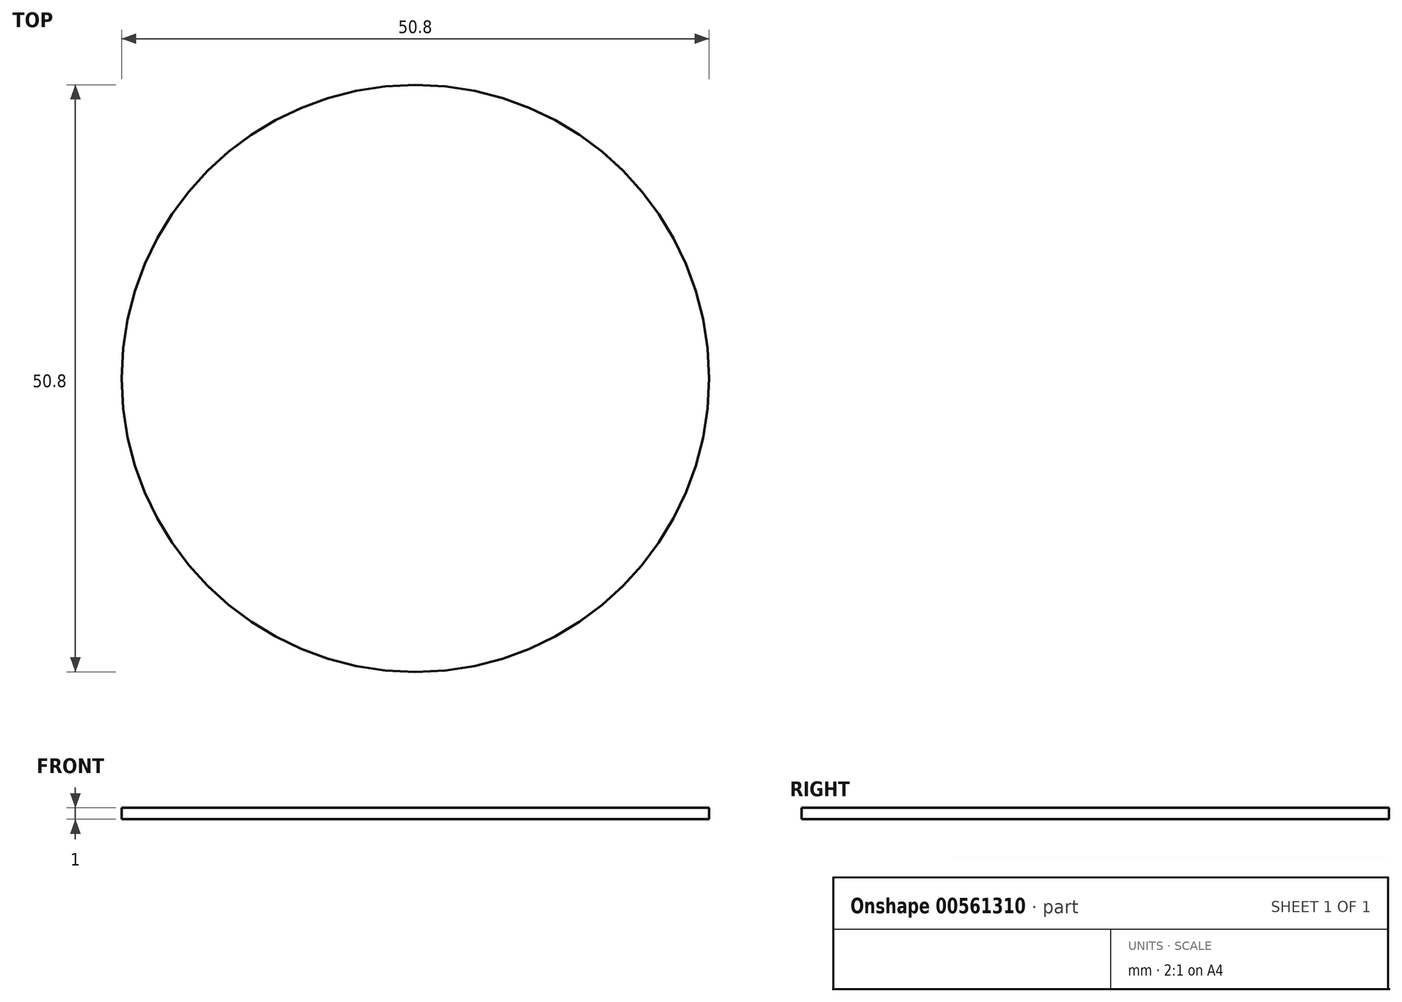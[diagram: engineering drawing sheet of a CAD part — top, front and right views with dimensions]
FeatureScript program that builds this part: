
annotation { "Feature Type Name" : "Feature", "Feature Type Description" : "" }
export const myFeature = defineFeature(function(context is Context, id is Id, definition is map)
    precondition{}
    {
        {
            var Q0;
            Q0=qCreatedBy(makeId("Top.planeOp"),FACE);
            var sketch = newSketch(context, id + "F0", { "sketchPlane" : qUnion([Q0])});
            skCircle(sketch, "E0", {"center": v(0, 0) * mm, "radius": 25.4 * mm});
            skSolve(sketch);
        }
        {
            var Q0;
            Q0 = qSketchRegion(id + "F0", true);
            extrude(context, id + "F1", {"entities" : qUnion([Q0]), "depth" : 1 * mm, "offsetDistance" : 25 * mm});
        }
    });
